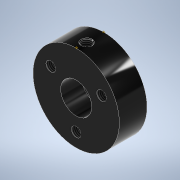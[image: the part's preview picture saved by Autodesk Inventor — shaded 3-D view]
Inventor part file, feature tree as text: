
AUTODESK INVENTOR PART (.ipt)
format: ipt  version: 2022 (Build 260153000, 153)  size: 189,440 bytes
history: native  units: mm
features: other x5, thread x4, extrude x3, sketch x2, plane x2, chamfer x1, projected_geometry x1
ambient origin geometry x8: Origin, YZ Plane, XZ Plane, XY Plane, X Axis, Y Axis, Z Axis, Center Point
bodies: Solid1 (feature_tree)
feature tree (18):
  sketch  "Sketch1"  dims[d0=25.0mm d1=17.0mm]
  extrude  "Extrusion1"  Depth=17.0mm
  extrude  "Extrusion2"  Depth=8.0mm
  other  "Work Axis1"
  other  "Work Axis2"
  plane  "Work Plane2"
  extrude  "Extrusion3"  Depth=2.8mm
  chamfer  "Chamfer1"  Distance=30.0mm Angle=360.0deg
  thread  "Thread1"  [1 undecoded]
  thread  "Thread2"  [1 undecoded]
  thread  "Thread3"  [1 undecoded]
  thread  "Thread4"  [1 undecoded]
  plane  "Work Plane1"
  other  "Work Point1"
  other  "Work Point2"
  other  "Work Axis3"
  sketch  "Sketch2"  dims[d2=9.0mm d3=8.0mm d4=2.8mm d5=30.0mm d7=360.0deg d9=8.0mm d10=0.0mm d11=6.0mm d12=0.0mm d13=90.0deg d14=2.8mm d16=6.0mm d17=0.0mm d18=0.2mm d19=2.0mm d20=45.0deg d21=5.0mm d22=8.0mm d23=0.0mm d24=8.0mm d25=0.0mm d26=8.0mm d27=0.0mm d28=8.046mm d29=0.0mm]
  projected_geometry  "Projected Loop1"
note: 4 required parameter values undecoded (feature->parameter linkage not recoverable at this tier; creation-order binding heuristic only, values carry confidence <= 0.55)
